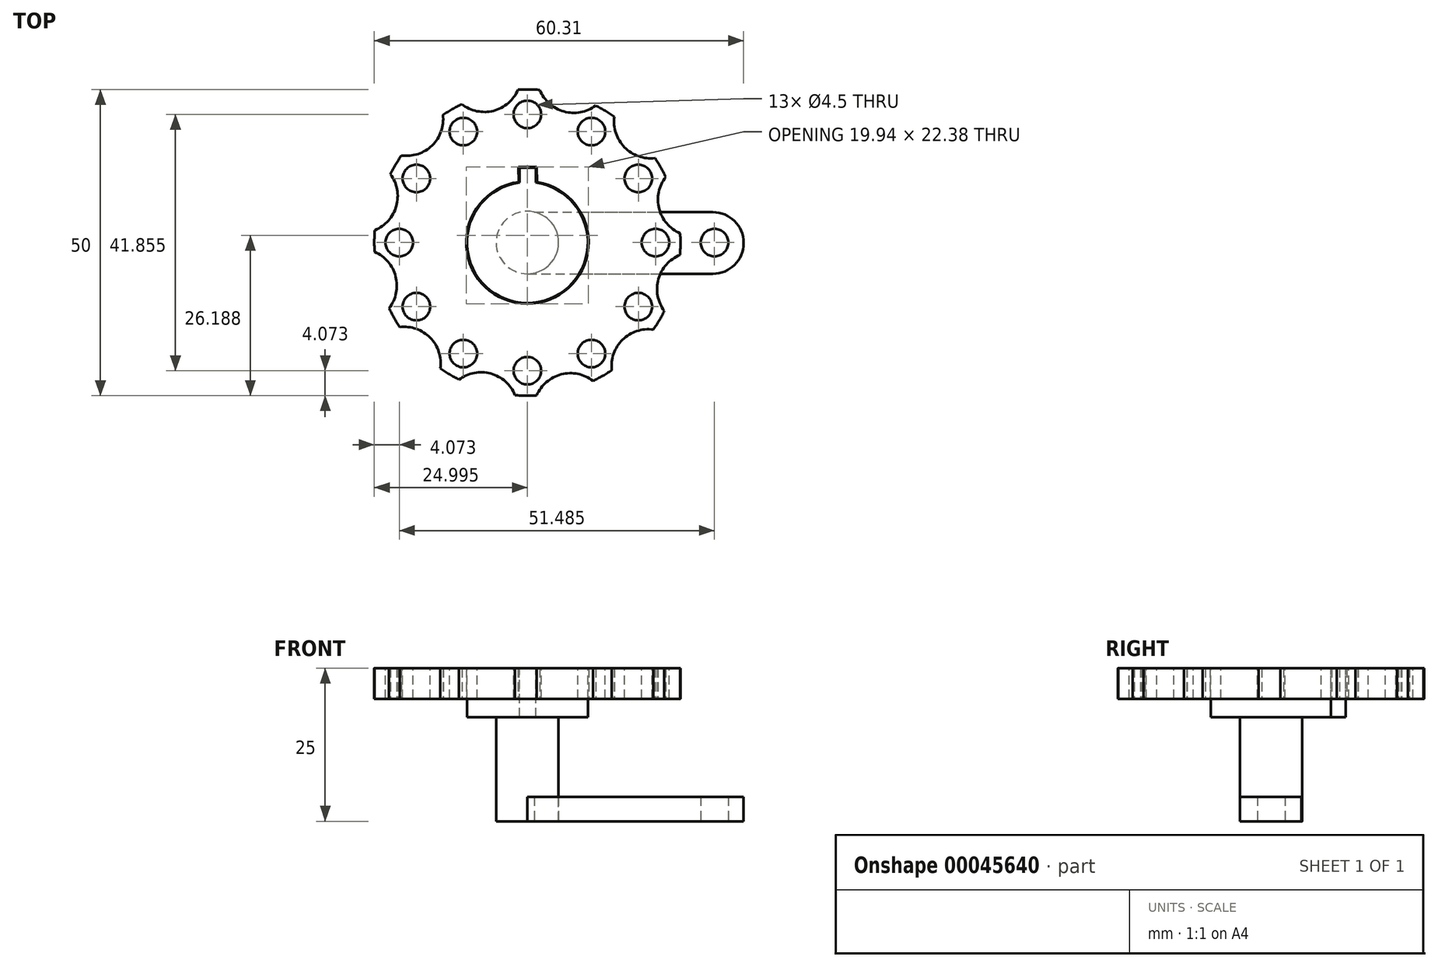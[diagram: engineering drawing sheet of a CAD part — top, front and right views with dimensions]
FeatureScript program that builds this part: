
annotation { "Feature Type Name" : "Feature", "Feature Type Description" : "" }
export const myFeature = defineFeature(function(context is Context, id is Id, definition is map)
    precondition{}
    {
        {
            var Q0;
            Q0=qCreatedBy(makeId("Top.planeOp"),FACE);
            var sketch = newSketch(context, id + "F0", { "sketchPlane" : qUnion([Q0])});
            skArc(sketch, "E0", {"start": v(-1.43, 9.9) * mm, "mid": v(-0.07, -10) * mm, "end": v(1.57, 9.88) * mm});
            skLineSegment(sketch, "E1.bottom", {"start": v(0, 0) * mm, "end": v(0, 0) * mm});
            skLineSegment(sketch, "E2.rect.bottom", {"start": v(1.54, 12.38) * mm, "end": v(-1.46, 12.38) * mm});
            skLineSegment(sketch, "E2.rect.left", {"start": v(1.54, 12.38) * mm, "end": v(1.57, 9.88) * mm});
            skLineSegment(sketch, "E2.rect.right", {"start": v(-1.46, 12.38) * mm, "end": v(-1.43, 9.9) * mm});
            skCircle(sketch, "E3", {"center": v(0, 0) * mm, "radius": 25 * mm});
            skPoint(sketch, "E4", {"position": v(-19.75, 20.15) * mm});
            skCircle(sketch, "E5", {"center": v(-27.18, 7.58) * mm, "radius": 6 * mm});
            skCircle(sketch, "E6.1.0", {"center": v(-27.33, -7.03) * mm, "radius": 6 * mm});
            skCircle(sketch, "E6.2.0", {"center": v(-20.15, -19.75) * mm, "radius": 6 * mm});
            skCircle(sketch, "E7.1.3.0", {"center": v(-7.58, -27.18) * mm, "radius": 6 * mm});
            skCircle(sketch, "E7.1.4.0", {"center": v(7.03, -27.33) * mm, "radius": 6 * mm});
            skCircle(sketch, "E7.1.5.0", {"center": v(19.75, -20.15) * mm, "radius": 6 * mm});
            skCircle(sketch, "E7.1.6.0", {"center": v(27.18, -7.58) * mm, "radius": 6 * mm});
            skCircle(sketch, "E7.1.7.0", {"center": v(27.33, 7.03) * mm, "radius": 6 * mm});
            skCircle(sketch, "E7.1.8.0", {"center": v(20.15, 19.75) * mm, "radius": 6 * mm});
            skCircle(sketch, "E7.1.9.0", {"center": v(7.58, 27.18) * mm, "radius": 6 * mm});
            skCircle(sketch, "E7.1.10.0", {"center": v(-7.03, 27.33) * mm, "radius": 6 * mm});
            skCircle(sketch, "E7.1.11.0", {"center": v(-19.75, 20.15) * mm, "radius": 6 * mm});
            skSolve(sketch);
        }
        {
            var Q0;
            Q0=makeQuery(id+"F0.imprint","IMPRINT",FACE,{"disambiguationData":[TD([[makeQuery(id+"F0.imprint","IMPRINT",EDGE,{"derivedFrom":sQuery(id+"F0.wireOp",EDGE,"E0")}),-1.0]])]});
            extrude(context, id + "F1", {"entities" : qUnion([Q0]), "depth" : 5 * mm, "hasSecondDirection" : true, "secondDirectionOppositeDirection" : true, "secondDirectionDepth" : 5 * mm});
        }
        {
            var Q0;
            Q0 = qSketchRegion(id + "F0", true);
            extrude(context, id + "F2", {"entities" : qUnion([Q0]), "operationType" : NewBodyOperationType.REMOVE, "depth" : 70 * mm});
        }
        {
            var Q0;
            Q0=qCreatedBy(makeId("Top.planeOp"),FACE);
            var sketch = newSketch(context, id + "F3", { "sketchPlane" : qUnion([Q0])});
            skCircle(sketch, "E8", {"center": v(-20.93, 0) * mm, "radius": 2.25 * mm});
            skCircle(sketch, "E9.1.0", {"center": v(-18.12, -10.46) * mm, "radius": 2.25 * mm});
            skCircle(sketch, "E9.2.0", {"center": v(-10.46, -18.12) * mm, "radius": 2.25 * mm});
            skCircle(sketch, "E9.3.0", {"center": v(0, -20.93) * mm, "radius": 2.25 * mm});
            skCircle(sketch, "E9.4.0", {"center": v(10.46, -18.12) * mm, "radius": 2.25 * mm});
            skCircle(sketch, "E9.5.0", {"center": v(18.12, -10.46) * mm, "radius": 2.25 * mm});
            skCircle(sketch, "E9.6.0", {"center": v(20.93, 0) * mm, "radius": 2.25 * mm});
            skCircle(sketch, "E9.7.0", {"center": v(18.12, 10.46) * mm, "radius": 2.25 * mm});
            skCircle(sketch, "E9.8.0", {"center": v(10.46, 18.12) * mm, "radius": 2.25 * mm});
            skCircle(sketch, "E9.9.0", {"center": v(0, 20.93) * mm, "radius": 2.25 * mm});
            skCircle(sketch, "E9.10.0", {"center": v(-10.46, 18.12) * mm, "radius": 2.25 * mm});
            skCircle(sketch, "E9.11.0", {"center": v(-18.12, 10.46) * mm, "radius": 2.25 * mm});
            skPoint(sketch, "E9.center", {"position": v(0, 0) * mm});
            skSolve(sketch);
        }
        {
            var Q0;
            Q0 = qSketchRegion(id + "F3", true);
            extrude(context, id + "F4", {"entities" : qUnion([Q0]), "operationType" : NewBodyOperationType.REMOVE, "endBound" : BoundingType.THROUGH_ALL, "oppositeDirection" : true, "depth" : 5 * mm});
        }
        {
            var Q0;
            {var subQ0=sQuery(id+"F0.wireOp",EDGE,"E3");var subQ1=sQuery(id+"F0.wireOp",EDGE,"E7.1.3.0");var subQ2=makeQuery(id+"F0.imprint","INTERSECT",VERTEX,{"disambiguationData":[OD(0.0)],"derivedFrom":[subQ1,subQ0]});Q0=makeQuery(id+"F0.imprint","IMPRINT",FACE,{"disambiguationData":[TD([[makeQuery(id+"F0.imprint","IMPRINT",EDGE,{"disambiguationData":[TD([[subQ2,-1.0]])],"derivedFrom":subQ1}),1.0]])]});}
            var Q1;
            {var subQ0=sQuery(id+"F0.wireOp",EDGE,"E3");var subQ1=sQuery(id+"F0.wireOp",EDGE,"E7.1.11.0");var subQ2=makeQuery(id+"F0.imprint","INTERSECT",VERTEX,{"disambiguationData":[OD(0.0)],"derivedFrom":[subQ1,subQ0]});Q1=makeQuery(id+"F0.imprint","IMPRINT",FACE,{"disambiguationData":[TD([[makeQuery(id+"F0.imprint","IMPRINT",EDGE,{"disambiguationData":[TD([[subQ2,-1.0]])],"derivedFrom":subQ1}),1.0]])]});}
            var Q2;
            {var subQ0=sQuery(id+"F0.wireOp",EDGE,"E3");var subQ1=sQuery(id+"F0.wireOp",EDGE,"E5");var subQ2=makeQuery(id+"F0.imprint","INTERSECT",VERTEX,{"disambiguationData":[OD(0.0)],"derivedFrom":[subQ1,subQ0]});Q2=makeQuery(id+"F0.imprint","IMPRINT",FACE,{"disambiguationData":[TD([[makeQuery(id+"F0.imprint","IMPRINT",EDGE,{"disambiguationData":[TD([[subQ2,1.0]])],"derivedFrom":subQ1}),1.0]])]});}
            var Q3;
            {var subQ0=sQuery(id+"F0.wireOp",EDGE,"E3");var subQ1=sQuery(id+"F0.wireOp",EDGE,"E5");var subQ2=makeQuery(id+"F0.imprint","INTERSECT",VERTEX,{"disambiguationData":[OD(0.0)],"derivedFrom":[subQ1,subQ0]});Q3=makeQuery(id+"F0.imprint","IMPRINT",FACE,{"disambiguationData":[TD([[makeQuery(id+"F0.imprint","IMPRINT",EDGE,{"disambiguationData":[TD([[subQ2,-1.0]])],"derivedFrom":subQ1}),1.0]])]});}
            var Q4;
            {var subQ0=sQuery(id+"F0.wireOp",EDGE,"E3");var subQ1=sQuery(id+"F0.wireOp",EDGE,"E7.1.11.0");var subQ2=makeQuery(id+"F0.imprint","INTERSECT",VERTEX,{"disambiguationData":[OD(0.0)],"derivedFrom":[subQ1,subQ0]});Q4=makeQuery(id+"F0.imprint","IMPRINT",FACE,{"disambiguationData":[TD([[makeQuery(id+"F0.imprint","IMPRINT",EDGE,{"disambiguationData":[TD([[subQ2,1.0]])],"derivedFrom":subQ1}),1.0]])]});}
            var Q5;
            {var subQ0=sQuery(id+"F0.wireOp",EDGE,"E3");var subQ1=sQuery(id+"F0.wireOp",EDGE,"E7.1.10.0");var subQ2=makeQuery(id+"F0.imprint","INTERSECT",VERTEX,{"disambiguationData":[OD(0.0)],"derivedFrom":[subQ1,subQ0]});Q5=makeQuery(id+"F0.imprint","IMPRINT",FACE,{"disambiguationData":[TD([[makeQuery(id+"F0.imprint","IMPRINT",EDGE,{"disambiguationData":[TD([[subQ2,-1.0]])],"derivedFrom":subQ1}),1.0]])]});}
            var Q6;
            {var subQ0=sQuery(id+"F0.wireOp",EDGE,"E3");var subQ1=sQuery(id+"F0.wireOp",EDGE,"E7.1.10.0");var subQ2=makeQuery(id+"F0.imprint","INTERSECT",VERTEX,{"disambiguationData":[OD(0.0)],"derivedFrom":[subQ1,subQ0]});Q6=makeQuery(id+"F0.imprint","IMPRINT",FACE,{"disambiguationData":[TD([[makeQuery(id+"F0.imprint","IMPRINT",EDGE,{"disambiguationData":[TD([[subQ2,1.0]])],"derivedFrom":subQ1}),1.0]])]});}
            var Q7;
            {var subQ0=sQuery(id+"F0.wireOp",EDGE,"E3");var subQ1=sQuery(id+"F0.wireOp",EDGE,"E7.1.9.0");var subQ2=makeQuery(id+"F0.imprint","INTERSECT",VERTEX,{"disambiguationData":[OD(0.0)],"derivedFrom":[subQ1,subQ0]});Q7=makeQuery(id+"F0.imprint","IMPRINT",FACE,{"disambiguationData":[TD([[makeQuery(id+"F0.imprint","IMPRINT",EDGE,{"disambiguationData":[TD([[subQ2,-1.0]])],"derivedFrom":subQ1}),1.0]])]});}
            var Q8;
            {var subQ0=sQuery(id+"F0.wireOp",EDGE,"E3");var subQ1=sQuery(id+"F0.wireOp",EDGE,"E7.1.9.0");var subQ2=makeQuery(id+"F0.imprint","INTERSECT",VERTEX,{"disambiguationData":[OD(0.0)],"derivedFrom":[subQ1,subQ0]});Q8=makeQuery(id+"F0.imprint","IMPRINT",FACE,{"disambiguationData":[TD([[makeQuery(id+"F0.imprint","IMPRINT",EDGE,{"disambiguationData":[TD([[subQ2,1.0]])],"derivedFrom":subQ1}),1.0]])]});}
            var Q9;
            {var subQ0=sQuery(id+"F0.wireOp",EDGE,"E3");var subQ1=sQuery(id+"F0.wireOp",EDGE,"E7.1.8.0");var subQ2=makeQuery(id+"F0.imprint","INTERSECT",VERTEX,{"disambiguationData":[OD(0.0)],"derivedFrom":[subQ1,subQ0]});Q9=makeQuery(id+"F0.imprint","IMPRINT",FACE,{"disambiguationData":[TD([[makeQuery(id+"F0.imprint","IMPRINT",EDGE,{"disambiguationData":[TD([[subQ2,-1.0]])],"derivedFrom":subQ1}),1.0]])]});}
            var Q10;
            {var subQ0=sQuery(id+"F0.wireOp",EDGE,"E3");var subQ1=sQuery(id+"F0.wireOp",EDGE,"E7.1.8.0");var subQ2=makeQuery(id+"F0.imprint","INTERSECT",VERTEX,{"disambiguationData":[OD(0.0)],"derivedFrom":[subQ1,subQ0]});Q10=makeQuery(id+"F0.imprint","IMPRINT",FACE,{"disambiguationData":[TD([[makeQuery(id+"F0.imprint","IMPRINT",EDGE,{"disambiguationData":[TD([[subQ2,1.0]])],"derivedFrom":subQ1}),1.0]])]});}
            var Q11;
            {var subQ0=sQuery(id+"F0.wireOp",EDGE,"E3");var subQ1=sQuery(id+"F0.wireOp",EDGE,"E7.1.7.0");var subQ2=makeQuery(id+"F0.imprint","INTERSECT",VERTEX,{"disambiguationData":[OD(0.0)],"derivedFrom":[subQ1,subQ0]});Q11=makeQuery(id+"F0.imprint","IMPRINT",FACE,{"disambiguationData":[TD([[makeQuery(id+"F0.imprint","IMPRINT",EDGE,{"disambiguationData":[TD([[subQ2,-1.0]])],"derivedFrom":subQ1}),1.0]])]});}
            var Q12;
            {var subQ0=sQuery(id+"F0.wireOp",EDGE,"E3");var subQ1=sQuery(id+"F0.wireOp",EDGE,"E7.1.7.0");var subQ2=makeQuery(id+"F0.imprint","INTERSECT",VERTEX,{"disambiguationData":[OD(0.0)],"derivedFrom":[subQ1,subQ0]});Q12=makeQuery(id+"F0.imprint","IMPRINT",FACE,{"disambiguationData":[TD([[makeQuery(id+"F0.imprint","IMPRINT",EDGE,{"disambiguationData":[TD([[subQ2,1.0]])],"derivedFrom":subQ1}),1.0]])]});}
            var Q13;
            {var subQ0=sQuery(id+"F0.wireOp",EDGE,"E3");var subQ1=sQuery(id+"F0.wireOp",EDGE,"E7.1.6.0");var subQ2=makeQuery(id+"F0.imprint","INTERSECT",VERTEX,{"disambiguationData":[OD(0.0)],"derivedFrom":[subQ1,subQ0]});Q13=makeQuery(id+"F0.imprint","IMPRINT",FACE,{"disambiguationData":[TD([[makeQuery(id+"F0.imprint","IMPRINT",EDGE,{"disambiguationData":[TD([[subQ2,1.0]])],"derivedFrom":subQ1}),1.0]])]});}
            var Q14;
            {var subQ0=sQuery(id+"F0.wireOp",EDGE,"E3");var subQ1=sQuery(id+"F0.wireOp",EDGE,"E7.1.6.0");var subQ2=makeQuery(id+"F0.imprint","INTERSECT",VERTEX,{"disambiguationData":[OD(0.0)],"derivedFrom":[subQ1,subQ0]});Q14=makeQuery(id+"F0.imprint","IMPRINT",FACE,{"disambiguationData":[TD([[makeQuery(id+"F0.imprint","IMPRINT",EDGE,{"disambiguationData":[TD([[subQ2,-1.0]])],"derivedFrom":subQ1}),1.0]])]});}
            var Q15;
            {var subQ0=sQuery(id+"F0.wireOp",EDGE,"E3");var subQ1=sQuery(id+"F0.wireOp",EDGE,"E7.1.5.0");var subQ2=makeQuery(id+"F0.imprint","INTERSECT",VERTEX,{"disambiguationData":[OD(0.0)],"derivedFrom":[subQ1,subQ0]});Q15=makeQuery(id+"F0.imprint","IMPRINT",FACE,{"disambiguationData":[TD([[makeQuery(id+"F0.imprint","IMPRINT",EDGE,{"disambiguationData":[TD([[subQ2,-1.0]])],"derivedFrom":subQ1}),1.0]])]});}
            var Q16;
            {var subQ0=sQuery(id+"F0.wireOp",EDGE,"E3");var subQ1=sQuery(id+"F0.wireOp",EDGE,"E7.1.5.0");var subQ2=makeQuery(id+"F0.imprint","INTERSECT",VERTEX,{"disambiguationData":[OD(0.0)],"derivedFrom":[subQ1,subQ0]});Q16=makeQuery(id+"F0.imprint","IMPRINT",FACE,{"disambiguationData":[TD([[makeQuery(id+"F0.imprint","IMPRINT",EDGE,{"disambiguationData":[TD([[subQ2,1.0]])],"derivedFrom":subQ1}),1.0]])]});}
            var Q17;
            {var subQ0=sQuery(id+"F0.wireOp",EDGE,"E3");var subQ1=sQuery(id+"F0.wireOp",EDGE,"E7.1.4.0");var subQ2=makeQuery(id+"F0.imprint","INTERSECT",VERTEX,{"disambiguationData":[OD(0.0)],"derivedFrom":[subQ1,subQ0]});Q17=makeQuery(id+"F0.imprint","IMPRINT",FACE,{"disambiguationData":[TD([[makeQuery(id+"F0.imprint","IMPRINT",EDGE,{"disambiguationData":[TD([[subQ2,-1.0]])],"derivedFrom":subQ1}),1.0]])]});}
            var Q18;
            {var subQ0=sQuery(id+"F0.wireOp",EDGE,"E3");var subQ1=sQuery(id+"F0.wireOp",EDGE,"E7.1.4.0");var subQ2=makeQuery(id+"F0.imprint","INTERSECT",VERTEX,{"disambiguationData":[OD(0.0)],"derivedFrom":[subQ1,subQ0]});Q18=makeQuery(id+"F0.imprint","IMPRINT",FACE,{"disambiguationData":[TD([[makeQuery(id+"F0.imprint","IMPRINT",EDGE,{"disambiguationData":[TD([[subQ2,1.0]])],"derivedFrom":subQ1}),1.0]])]});}
            var Q19;
            {var subQ0=sQuery(id+"F0.wireOp",EDGE,"E3");var subQ1=sQuery(id+"F0.wireOp",EDGE,"E7.1.3.0");var subQ2=makeQuery(id+"F0.imprint","INTERSECT",VERTEX,{"disambiguationData":[OD(0.0)],"derivedFrom":[subQ1,subQ0]});Q19=makeQuery(id+"F0.imprint","IMPRINT",FACE,{"disambiguationData":[TD([[makeQuery(id+"F0.imprint","IMPRINT",EDGE,{"disambiguationData":[TD([[subQ2,1.0]])],"derivedFrom":subQ1}),1.0]])]});}
            var Q20;
            {var subQ0=sQuery(id+"F0.wireOp",EDGE,"E3");var subQ1=sQuery(id+"F0.wireOp",EDGE,"E6.2.0");var subQ2=makeQuery(id+"F0.imprint","INTERSECT",VERTEX,{"disambiguationData":[OD(0.0)],"derivedFrom":[subQ1,subQ0]});Q20=makeQuery(id+"F0.imprint","IMPRINT",FACE,{"disambiguationData":[TD([[makeQuery(id+"F0.imprint","IMPRINT",EDGE,{"disambiguationData":[TD([[subQ2,-1.0]])],"derivedFrom":subQ1}),1.0]])]});}
            var Q21;
            {var subQ0=sQuery(id+"F0.wireOp",EDGE,"E3");var subQ1=sQuery(id+"F0.wireOp",EDGE,"E6.2.0");var subQ2=makeQuery(id+"F0.imprint","INTERSECT",VERTEX,{"disambiguationData":[OD(0.0)],"derivedFrom":[subQ1,subQ0]});Q21=makeQuery(id+"F0.imprint","IMPRINT",FACE,{"disambiguationData":[TD([[makeQuery(id+"F0.imprint","IMPRINT",EDGE,{"disambiguationData":[TD([[subQ2,1.0]])],"derivedFrom":subQ1}),1.0]])]});}
            var Q22;
            {var subQ0=sQuery(id+"F0.wireOp",EDGE,"E3");var subQ1=sQuery(id+"F0.wireOp",EDGE,"E6.1.0");var subQ2=makeQuery(id+"F0.imprint","INTERSECT",VERTEX,{"disambiguationData":[OD(0.0)],"derivedFrom":[subQ1,subQ0]});Q22=makeQuery(id+"F0.imprint","IMPRINT",FACE,{"disambiguationData":[TD([[makeQuery(id+"F0.imprint","IMPRINT",EDGE,{"disambiguationData":[TD([[subQ2,-1.0]])],"derivedFrom":subQ1}),1.0]])]});}
            var Q23;
            {var subQ0=sQuery(id+"F0.wireOp",EDGE,"E3");var subQ1=sQuery(id+"F0.wireOp",EDGE,"E6.1.0");var subQ2=makeQuery(id+"F0.imprint","INTERSECT",VERTEX,{"disambiguationData":[OD(0.0)],"derivedFrom":[subQ1,subQ0]});Q23=makeQuery(id+"F0.imprint","IMPRINT",FACE,{"disambiguationData":[TD([[makeQuery(id+"F0.imprint","IMPRINT",EDGE,{"disambiguationData":[TD([[subQ2,1.0]])],"derivedFrom":subQ1}),1.0]])]});}
            extrude(context, id + "F5", {"entities" : qUnion([Q0, Q1, Q2, Q3, Q4, Q5, Q6, Q7, Q8, Q9, Q10, Q11, Q12, Q13, Q14, Q15, Q16, Q17, Q18, Q19, Q20, Q21, Q22, Q23]), "operationType" : NewBodyOperationType.REMOVE, "oppositeDirection" : true, "depth" : 25 * mm});
        }
        {
            var Q0;
            Q0=qCreatedBy(makeId("Top.planeOp"),FACE);
            var sketch = newSketch(context, id + "F6", { "sketchPlane" : qUnion([Q0])});
            skArc(sketch, "E10", {"start": v(-1.27, 9.8) * mm, "mid": v(-0.06, -9.87) * mm, "end": v(1.38, 9.78) * mm});
            skPoint(sketch, "E11", {"position": v(-1.27, 9.8) * mm});
            skLineSegment(sketch, "E12.top", {"start": v(-1.27, 12.19) * mm, "end": v(1.38, 12.19) * mm});
            skLineSegment(sketch, "E12.left", {"start": v(-1.27, 9.8) * mm, "end": v(-1.27, 12.19) * mm});
            skLineSegment(sketch, "E12.right", {"start": v(1.38, 9.78) * mm, "end": v(1.38, 12.19) * mm});
            skCircle(sketch, "E13", {"center": v(0, 0) * mm, "radius": 5.1 * mm});
            skSolve(sketch);
        }
        {
            var Q0;
            Q0=makeQuery(id+"F6.imprint","IMPRINT",FACE,{"disambiguationData":[TD([[makeQuery(id+"F6.imprint","IMPRINT",EDGE,{"derivedFrom":sQuery(id+"F6.wireOp",EDGE,"E10")}),1.0]])]});
            extrude(context, id + "F7", {"entities" : qUnion([Q0]), "oppositeDirection" : true, "depth" : 8 * mm});
        }
        {
            var Q0;
            Q0=makeQuery(id+"F6.imprint","IMPRINT",FACE,{"disambiguationData":[TD([[makeQuery(id+"F6.imprint","IMPRINT",EDGE,{"derivedFrom":sQuery(id+"F6.wireOp",EDGE,"E13")}),1.0]])]});
            var Q1;
            Q1=sQuery(id+"F6.wireOp",EDGE,"E13");
            extrude(context, id + "F8", {"entities" : qUnion([Q0]), "operationType" : NewBodyOperationType.ADD, "surfaceEntities" : qUnion([Q1]), "oppositeDirection" : true, "depth" : 25 * mm});
        }
        {
            var Q0;
            Q0=makeQuery(id+"F8.opExtrude","CAP_FACE",FACE,{"disambiguationData":[OSD([sQuery(id+"F6.wireOp",EDGE,"E13")])],"isStart":false});
            var sketch = newSketch(context, id + "F9", { "sketchPlane" : qUnion([Q0])});
            skArc(sketch, "E14", {"start": v(0, 5) * mm, "mid": v(-5, -0.27) * mm, "end": v(0.54, -4.97) * mm});
            skPoint(sketch, "E15", {"position": v(0, 5.1) * mm});
            skLineSegment(sketch, "E16.bottom", {"start": v(0, 5.1) * mm, "end": v(35.3, 5.1) * mm});
            skLineSegment(sketch, "E16.top", {"start": v(0.54, -4.97) * mm, "end": v(35.3, -4.97) * mm});
            skLineSegment(sketch, "E16.left", {"start": v(0, 5.1) * mm, "end": v(0, 5) * mm});
            skLineSegment(sketch, "E16.right", {"start": v(35.3, 5.1) * mm, "end": v(35.3, -4.97) * mm});
            skSolve(sketch);
        }
        {
            var Q0;
            {var subQ0=sQuery(id+"F9.wireOp",EDGE,"E16.bottom");Q0=makeQuery(id+"F9.imprint","IMPRINT",FACE,{"disambiguationData":[TD([[makeQuery(id+"F9.imprint","IMPRINT",EDGE,{"derivedFrom":subQ0}),-1.0]])]});}
            extrude(context, id + "F10", {"entities" : qUnion([Q0]), "oppositeDirection" : true, "depth" : 4 * mm});
        }
        {
            var Q0;
            {var subQ0=sQuery(id+"F9.wireOp",EDGE,"E16.bottom");Q0=makeQuery(id+"F9.imprint","IMPRINT",FACE,{"disambiguationData":[TD([[makeQuery(id+"F9.imprint","IMPRINT",EDGE,{"derivedFrom":subQ0}),-1.0]])]});}
            var sketch = newSketch(context, id + "F11", { "sketchPlane" : qUnion([Q0])});
            skPoint(sketch, "E17", {"position": v(30.56, 0) * mm});
            skCircle(sketch, "E18", {"center": v(30.56, 0) * mm, "radius": 2.25 * mm});
            skSolve(sketch);
        }
        {
            var Q0;
            Q0 = qSketchRegion(id + "F11", true);
            extrude(context, id + "F12", {"entities" : qUnion([Q0]), "operationType" : NewBodyOperationType.REMOVE, "oppositeDirection" : true, "depth" : 5 * mm});
        }
        {
            var Q0;
            Q0=makeQuery(id+"F10.opExtrude","SWEPT_EDGE",EDGE,{"disambiguationData":[OSD([sQuery(id+"F9.wireOp",EDGE,"E16.top"),sQuery(id+"F9.wireOp",EDGE,"E16.right")])]});
            fillet(context, id + "F13", {"entities" : qUnion([Q0]), "radius" : 5 * mm, "tangentPropagation" : true, "allowEdgeOverflow" : false});
        }
        {
            var Q0;
            Q0=makeQuery(id+"F10.opExtrude","SWEPT_EDGE",EDGE,{"disambiguationData":[OSD([sQuery(id+"F9.wireOp",EDGE,"E16.bottom"),sQuery(id+"F9.wireOp",EDGE,"E16.right")])]});
            fillet(context, id + "F14", {"entities" : qUnion([Q0]), "radius" : 5 * mm, "tangentPropagation" : true, "allowEdgeOverflow" : false});
        }
    });
